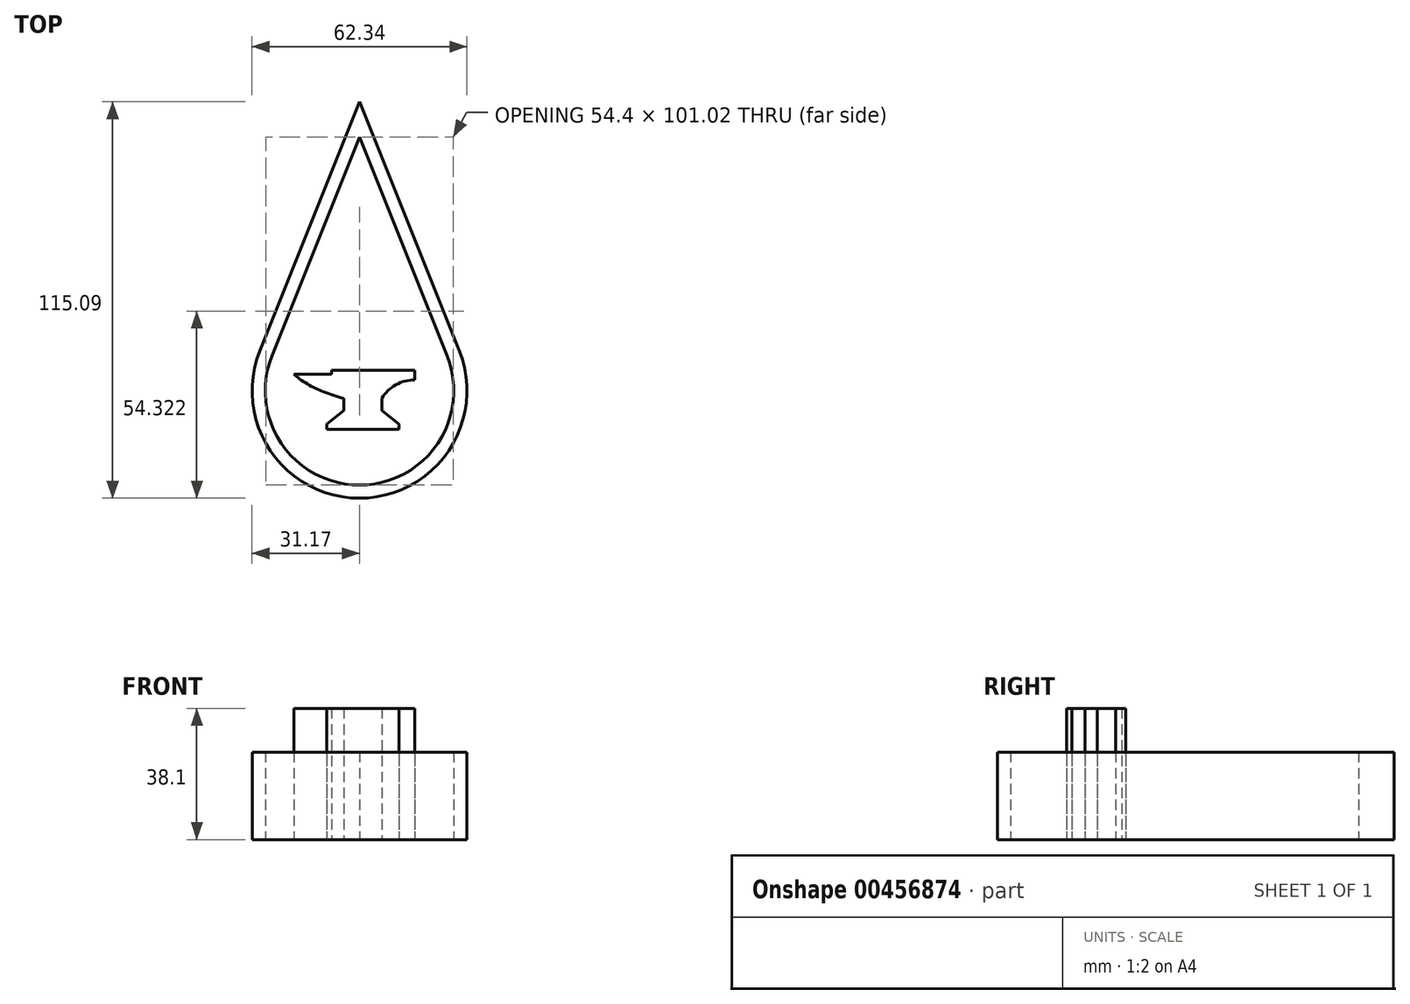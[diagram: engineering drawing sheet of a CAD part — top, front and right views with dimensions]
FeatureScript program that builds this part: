
annotation { "Feature Type Name" : "Feature", "Feature Type Description" : "" }
export const myFeature = defineFeature(function(context is Context, id is Id, definition is map)
    precondition{}
    {
        {
            var Q0;
            Q0=qCreatedBy(makeId("Top.planeOp"),FACE);
            var sketch = newSketch(context, id + "F0", { "sketchPlane" : qUnion([Q0])});
            skLineSegment(sketch, "E0", {"start": v(0, 0) * mm, "end": v(-25.4, -63.5) * mm});
            skLineSegment(sketch, "E1", {"start": v(-25.4, -63.5) * mm, "end": v(0, 0) * mm, "construction": true});
            skLineSegment(sketch, "E2", {"start": v(0, 0) * mm, "end": v(0, -73.66) * mm, "construction": true});
            skArc(sketch, "E3", {"start": v(-25.4, -63.5) * mm, "mid": v(-22.65, -89) * mm, "end": v(0, -101.02) * mm});
            skLineSegment(sketch, "E4.MirrorCS", {"start": v(0, 0) * mm, "end": v(25.4, -63.5) * mm});
            skArc(sketch, "E5.MirrorCS", {"start": v(25.4, -63.5) * mm, "mid": v(22.65, -89) * mm, "end": v(0, -101.02) * mm});
            skLineSegment(sketch, "E6.0", {"start": v(0, 10.26) * mm, "end": v(28.94, -62.09) * mm});
            skLineSegment(sketch, "E6.1", {"start": v(-28.94, -62.09) * mm, "end": v(0, 10.26) * mm});
            skArc(sketch, "E6.2", {"start": v(-28.94, -62.09) * mm, "mid": v(-25.8, -91.13) * mm, "end": v(0, -104.83) * mm});
            skArc(sketch, "E6.3", {"start": v(28.94, -62.09) * mm, "mid": v(25.8, -91.13) * mm, "end": v(0, -104.83) * mm});
            skSolve(sketch);
        }
        {
            var Q0;
            Q0=qCreatedBy(makeId("Top.planeOp"),FACE);
            var sketch = newSketch(context, id + "F1", { "sketchPlane" : qUnion([Q0])});
            skLineSegment(sketch, "E7", {"start": v(-5.42, -73.9) * mm, "end": v(10.67, -73.9) * mm});
            skLineSegment(sketch, "E8", {"start": v(10.67, -73.9) * mm, "end": v(10.67, -73.9) * mm});
            skLineSegment(sketch, "E9", {"start": v(-5.42, -73.9) * mm, "end": v(-5.42, -74.65) * mm});
            skLineSegment(sketch, "E10", {"start": v(-12.7, -74.65) * mm, "end": v(-5.42, -74.65) * mm});
            skLineSegment(sketch, "E11", {"start": v(7.62, -85.32) * mm, "end": v(-6.35, -85.32) * mm});
            skLineSegment(sketch, "E12.top", {"start": v(-6.35, -84.29) * mm, "end": v(7.62, -84.29) * mm});
            skLineSegment(sketch, "E12.left", {"start": v(-6.35, -85.32) * mm, "end": v(-6.35, -84.29) * mm});
            skLineSegment(sketch, "E12.right", {"start": v(7.62, -85.32) * mm, "end": v(7.62, -84.29) * mm});
            skLineSegment(sketch, "E13", {"start": v(7.62, -84.29) * mm, "end": v(4.32, -81.72) * mm});
            skLineSegment(sketch, "E14", {"start": v(4.32, -81.72) * mm, "end": v(4.32, -79.34) * mm});
            skLineSegment(sketch, "E15", {"start": v(-3.05, -79.34) * mm, "end": v(-3.05, -81.72) * mm});
            skLineSegment(sketch, "E16", {"start": v(-3.05, -81.72) * mm, "end": v(-6.35, -84.29) * mm});
            skFitSpline(sketch, "E17", {"points": [v(-12.7, -74.65) * mm, v(-3.05, -79.34) * mm], "startDerivative": vector(5.47, -5.48) * mm, "endDerivative": vector(11.48, -2.8) * mm});
            skLineSegment(sketch, "E18", {"start": v(10.67, -73.9) * mm, "end": v(10.67, -75.77) * mm});
            skArc(sketch, "E19", {"start": v(10.67, -75.77) * mm, "mid": v(7.03, -76.73) * mm, "end": v(4.32, -79.34) * mm});
            skSolve(sketch);
        }
        {
            var Q0;
            Q0=makeQuery(id+"F0.imprint","IMPRINT",FACE,{"disambiguationData":[TD([[makeQuery(id+"F0.imprint","IMPRINT",EDGE,{"derivedFrom":sQuery(id+"F0.wireOp",EDGE,"E0")}),-1.0]])]});
            var Q1;
            Q1=makeQuery(id+"F1.imprint","IMPRINT",FACE,{"disambiguationData":[TD([[makeQuery(id+"F1.imprint","IMPRINT",EDGE,{"derivedFrom":sQuery(id+"F1.wireOp",EDGE,"E7")}),-1.0]])]});
            var Q2;
            Q2=makeQuery(id+"F1.imprint","IMPRINT",FACE,{"disambiguationData":[TD([[makeQuery(id+"F1.imprint","IMPRINT",EDGE,{"derivedFrom":sQuery(id+"F1.wireOp",EDGE,"E11")}),-1.0]])]});
            extrude(context, id + "F2", {"entities" : qUnion([Q0, Q1, Q2]), "depth" : 25.4 * mm});
        }
        {
            var Q0;
            Q0=makeQuery(id+"F2.opExtrude","SWEPT_BODY",BODY,{"disambiguationData":[OSD([sQuery(id+"F1.wireOp",EDGE,"E7"),sQuery(id+"F1.wireOp",EDGE,"E9"),sQuery(id+"F1.wireOp",EDGE,"E10"),sQuery(id+"F1.wireOp",EDGE,"E11"),sQuery(id+"F1.wireOp",EDGE,"E12.left"),sQuery(id+"F1.wireOp",EDGE,"E12.right"),sQuery(id+"F1.wireOp",EDGE,"E13"),sQuery(id+"F1.wireOp",EDGE,"E14"),sQuery(id+"F1.wireOp",EDGE,"E15"),sQuery(id+"F1.wireOp",EDGE,"E16"),sQuery(id+"F1.wireOp",EDGE,"E17"),sQuery(id+"F1.wireOp",EDGE,"E18"),sQuery(id+"F1.wireOp",EDGE,"E19")])]});
            var Q1;
            Q1=qCreatedBy(makeId("Origin.pointOp"),VERTEX);
            transform(context, id + "F3", {"entities" : qUnion([Q0]), "transformType" : TransformType.SCALE_UNIFORMLY, "scale" : 1.5, "scalePoint" : qUnion([Q1]), "makeCopy" : false});
        }
        {
            var Q0;
            Q0=makeQuery(id+"F2.opExtrude","SWEPT_BODY",BODY,{"disambiguationData":[OSD([sQuery(id+"F1.wireOp",EDGE,"E7"),sQuery(id+"F1.wireOp",EDGE,"E9"),sQuery(id+"F1.wireOp",EDGE,"E10"),sQuery(id+"F1.wireOp",EDGE,"E11"),sQuery(id+"F1.wireOp",EDGE,"E12.left"),sQuery(id+"F1.wireOp",EDGE,"E12.right"),sQuery(id+"F1.wireOp",EDGE,"E13"),sQuery(id+"F1.wireOp",EDGE,"E14"),sQuery(id+"F1.wireOp",EDGE,"E15"),sQuery(id+"F1.wireOp",EDGE,"E16"),sQuery(id+"F1.wireOp",EDGE,"E17"),sQuery(id+"F1.wireOp",EDGE,"E18"),sQuery(id+"F1.wireOp",EDGE,"E19")])]});
            transform(context, id + "F4", {"entities" : qUnion([Q0]), "transformType" : TransformType.TRANSLATION_3D, "dx" : 0 * mm, "dy" : 43.18 * mm, "dz" : 0 * mm, "makeCopy" : false});
        }
    });
